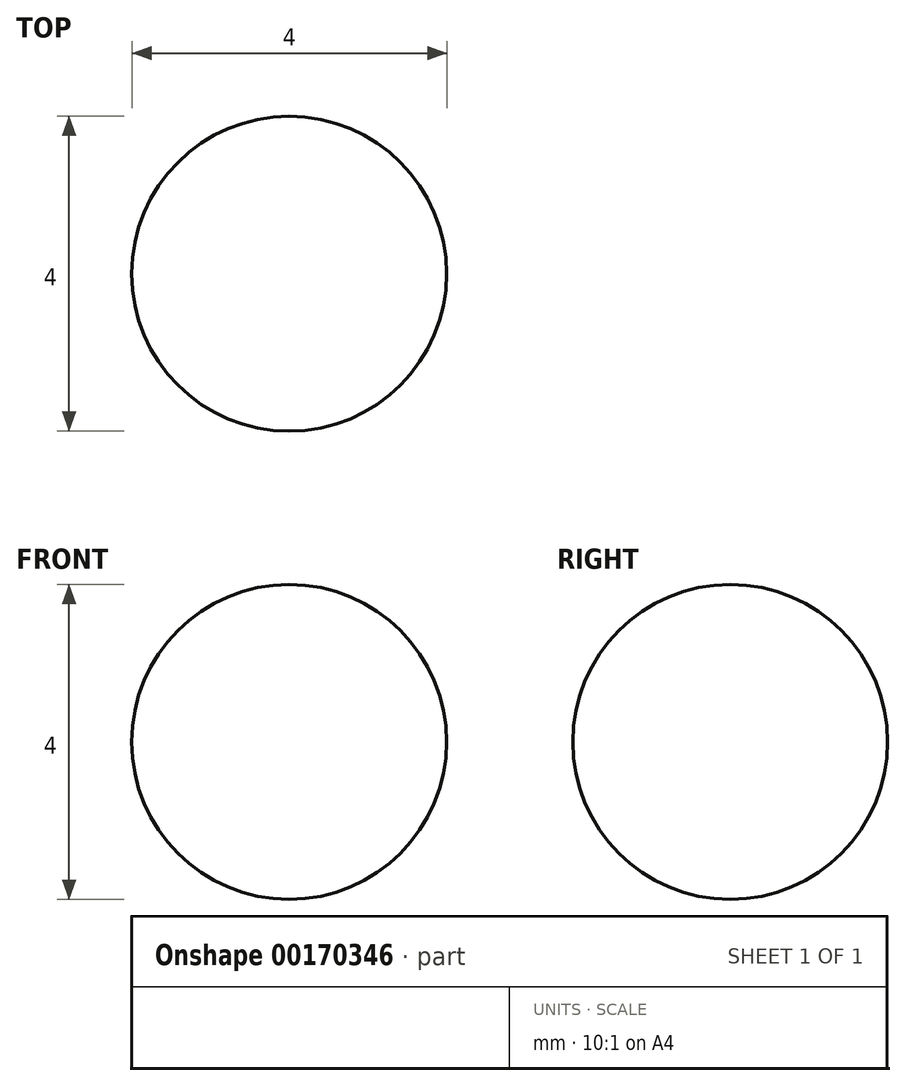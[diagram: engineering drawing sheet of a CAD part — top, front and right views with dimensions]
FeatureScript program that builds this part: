
annotation { "Feature Type Name" : "Feature", "Feature Type Description" : "" }
export const myFeature = defineFeature(function(context is Context, id is Id, definition is map)
    precondition{}
    {
        {
            var Q0;
            Q0=qCreatedBy(makeId("Top.planeOp"),FACE);
            var sketch = newSketch(context, id + "F0", { "sketchPlane" : qUnion([Q0])});
            skLineSegment(sketch, "E0", {"start": v(27.05, 22.85) * mm, "end": v(27.05, 18.85) * mm});
            skArc(sketch, "E1", {"start": v(27.05, 18.85) * mm, "mid": v(29.05, 20.85) * mm, "end": v(27.05, 22.85) * mm});
            skSolve(sketch);
        }
        {
            var Q0;
            Q0=makeQuery(id+"F0.imprint","IMPRINT",FACE,{"disambiguationData":[TD([[makeQuery(id+"F0.imprint","IMPRINT",EDGE,{"derivedFrom":sQuery(id+"F0.wireOp",EDGE,"E0")}),1.0]])]});
            var Q1;
            Q1=sQuery(id+"F0.wireOp",EDGE,"E0");
            revolve(context, id + "F1", {"entities" : qUnion([Q0]), "axis" : qUnion([Q1]), "revolveType" : RevolveType.FULL});
        }
    });
